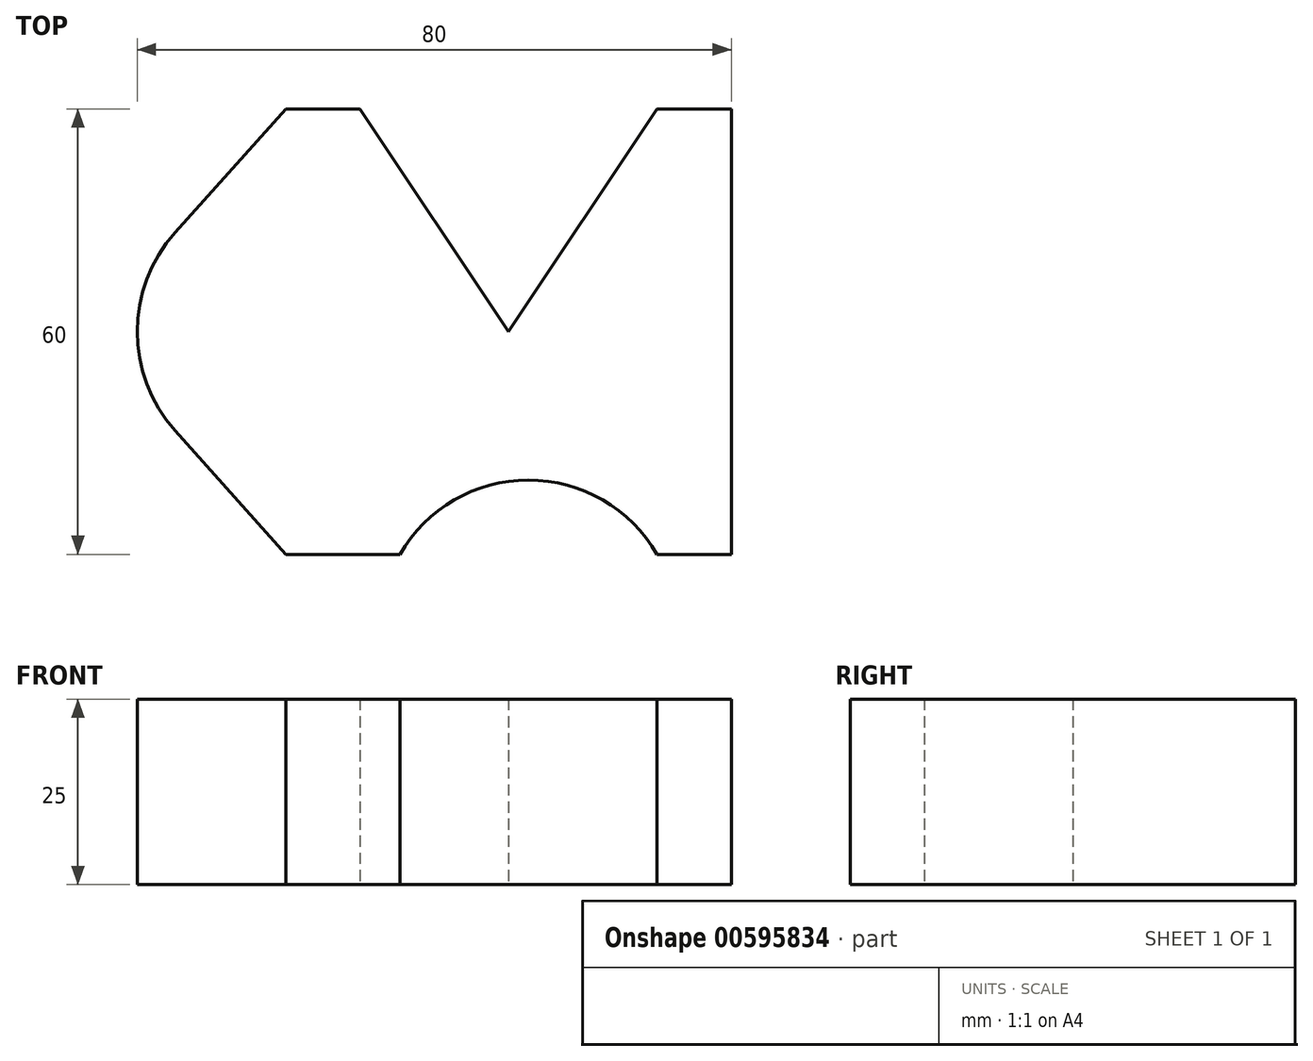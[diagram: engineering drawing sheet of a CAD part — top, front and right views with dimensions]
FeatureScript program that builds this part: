
annotation { "Feature Type Name" : "Feature", "Feature Type Description" : "" }
export const myFeature = defineFeature(function(context is Context, id is Id, definition is map)
    precondition{}
    {
        {
            var Q0;
            Q0=qCreatedBy(makeId("Top.planeOp"),FACE);
            var sketch = newSketch(context, id + "F0", { "sketchPlane" : qUnion([Q0])});
            skLineSegment(sketch, "E0", {"start": v(0, 0) * mm, "end": v(20, 30) * mm});
            skLineSegment(sketch, "E1", {"start": v(20, 30) * mm, "end": v(30, 30) * mm});
            skLineSegment(sketch, "E2", {"start": v(30, 30) * mm, "end": v(30, -30) * mm});
            skLineSegment(sketch, "E3", {"start": v(30, -30) * mm, "end": v(20, -30) * mm});
            skArc(sketch, "E4", {"start": v(20, -30) * mm, "mid": v(2.68, -20) * mm, "end": v(-14.64, -30) * mm});
            skLineSegment(sketch, "E5", {"start": v(-14.64, -30) * mm, "end": v(-30, -30) * mm});
            skLineSegment(sketch, "E6", {"start": v(-30, -30) * mm, "end": v(-44.9, -13.33) * mm});
            skArc(sketch, "E7", {"start": v(-44.9, 13.33) * mm, "mid": v(-50, 0) * mm, "end": v(-44.9, -13.33) * mm});
            skLineSegment(sketch, "E8", {"start": v(-44.9, 13.33) * mm, "end": v(-30, 30) * mm});
            skLineSegment(sketch, "E9", {"start": v(-30, 30) * mm, "end": v(-20, 30) * mm});
            skLineSegment(sketch, "E10", {"start": v(-20, 30) * mm, "end": v(0, 0) * mm});
            skSolve(sketch);
        }
        {
            var Q0;
            Q0=makeQuery(id+"F0.imprint","IMPRINT",FACE,{"disambiguationData":[TD([[makeQuery(id+"F0.imprint","IMPRINT",EDGE,{"derivedFrom":sQuery(id+"F0.wireOp",EDGE,"E0")}),-1.0]])]});
            extrude(context, id + "F1", {"entities" : qUnion([Q0]), "depth" : 25 * mm, "offsetDistance" : 25 * mm});
        }
    });
